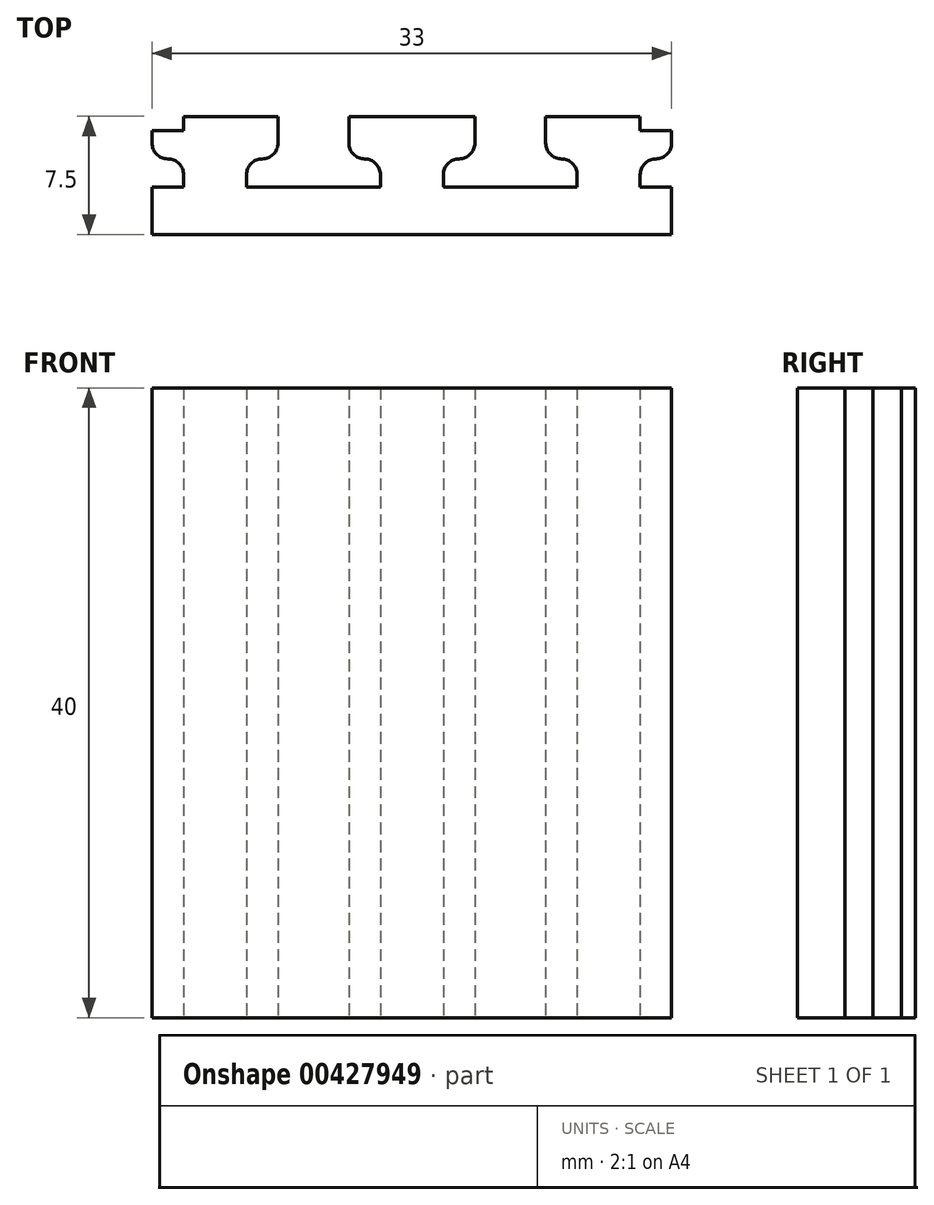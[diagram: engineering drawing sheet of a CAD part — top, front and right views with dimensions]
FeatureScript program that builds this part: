
annotation { "Feature Type Name" : "Feature", "Feature Type Description" : "" }
export const myFeature = defineFeature(function(context is Context, id is Id, definition is map)
    precondition{}
    {
        {
            var Q0;
            Q0=qCreatedBy(makeId("Top.planeOp"),FACE);
            var sketch = newSketch(context, id + "F0", { "sketchPlane" : qUnion([Q0])});
            skLineSegment(sketch, "E0.bottom", {"start": v(-2, 0.2) * mm, "end": v(2, 0.2) * mm});
            skLineSegment(sketch, "E0.top", {"start": v(-2, -3.4) * mm, "end": v(2, -3.4) * mm});
            skLineSegment(sketch, "E0.left", {"start": v(-2, 0.2) * mm, "end": v(-2, -3.4) * mm});
            skLineSegment(sketch, "E0.right", {"start": v(2, 0.2) * mm, "end": v(2, -3.4) * mm});
            skLineSegment(sketch, "E1.bottom", {"start": v(-4, 0.2) * mm, "end": v(4, 0.2) * mm});
            skLineSegment(sketch, "E1.top", {"start": v(-4, -1.6) * mm, "end": v(4, -1.6) * mm});
            skLineSegment(sketch, "E1.left", {"start": v(-4, 0.2) * mm, "end": v(-4, -1.6) * mm});
            skLineSegment(sketch, "E1.right", {"start": v(4, 0.2) * mm, "end": v(4, -1.6) * mm});
            skLineSegment(sketch, "E2.1.0.0", {"start": v(8.5, 0.2) * mm, "end": v(16.5, 0.2) * mm});
            skLineSegment(sketch, "E2.1.0.1", {"start": v(16.5, 0.2) * mm, "end": v(16.5, -1.6) * mm});
            skLineSegment(sketch, "E2.1.0.2", {"start": v(8.5, -1.6) * mm, "end": v(16.5, -1.6) * mm});
            skLineSegment(sketch, "E2.1.0.3", {"start": v(14.5, 0.2) * mm, "end": v(14.5, -3.4) * mm});
            skLineSegment(sketch, "E2.1.0.4", {"start": v(10.5, -3.4) * mm, "end": v(14.5, -3.4) * mm});
            skLineSegment(sketch, "E2.1.0.5", {"start": v(10.5, 0.2) * mm, "end": v(10.5, -3.4) * mm});
            skLineSegment(sketch, "E2.1.0.6", {"start": v(8.5, 0.2) * mm, "end": v(8.5, -1.6) * mm});
            skLineSegment(sketch, "E2.2.0.0", {"start": v(21, 0.2) * mm, "end": v(29, 0.2) * mm});
            skLineSegment(sketch, "E2.2.0.1", {"start": v(29, 0.2) * mm, "end": v(29, -1.6) * mm});
            skLineSegment(sketch, "E2.2.0.2", {"start": v(21, -1.6) * mm, "end": v(29, -1.6) * mm});
            skLineSegment(sketch, "E2.2.0.3", {"start": v(27, 0.2) * mm, "end": v(27, -3.4) * mm});
            skLineSegment(sketch, "E2.2.0.4", {"start": v(23, -3.4) * mm, "end": v(27, -3.4) * mm});
            skLineSegment(sketch, "E2.2.0.5", {"start": v(23, 0.2) * mm, "end": v(23, -3.4) * mm});
            skLineSegment(sketch, "E2.2.0.6", {"start": v(21, 0.2) * mm, "end": v(21, -1.6) * mm});
            skLineSegment(sketch, "E2.direction1", {"start": v(-4, 0.2) * mm, "end": v(8.5, 0.2) * mm, "construction": true});
            skLineSegment(sketch, "E3.bottom", {"start": v(-4, -3.4) * mm, "end": v(29, -3.4) * mm});
            skLineSegment(sketch, "E3.top", {"start": v(-4, -6.4) * mm, "end": v(29, -6.4) * mm});
            skLineSegment(sketch, "E3.left", {"start": v(-4, -3.4) * mm, "end": v(-4, -6.4) * mm});
            skLineSegment(sketch, "E3.right", {"start": v(29, -3.4) * mm, "end": v(29, -6.4) * mm});
            skLineSegment(sketch, "E4.bottom", {"start": v(16.5, 0.2) * mm, "end": v(8.5, 0.2) * mm});
            skLineSegment(sketch, "E4.top", {"start": v(16.5, 1.1) * mm, "end": v(8.5, 1.1) * mm});
            skLineSegment(sketch, "E4.left", {"start": v(16.5, 0.2) * mm, "end": v(16.5, 1.1) * mm});
            skLineSegment(sketch, "E4.right", {"start": v(8.5, 0.2) * mm, "end": v(8.5, 1.1) * mm});
            skLineSegment(sketch, "E5.bottom", {"start": v(4, 0.2) * mm, "end": v(-2, 0.2) * mm});
            skLineSegment(sketch, "E5.top", {"start": v(4, 1.1) * mm, "end": v(-2, 1.1) * mm});
            skLineSegment(sketch, "E5.left", {"start": v(4, 0.2) * mm, "end": v(4, 1.1) * mm});
            skLineSegment(sketch, "E5.right", {"start": v(-2, 0.2) * mm, "end": v(-2, 1.1) * mm});
            skPoint(sketch, "E6.oppositeSnap0", {"position": v(1, 1.1) * mm});
            skLineSegment(sketch, "E6.bottom", {"start": v(21, 0.2) * mm, "end": v(27, 0.2) * mm});
            skLineSegment(sketch, "E6.top", {"start": v(21, 1.1) * mm, "end": v(27, 1.1) * mm});
            skLineSegment(sketch, "E6.left", {"start": v(21, 0.2) * mm, "end": v(21, 1.1) * mm});
            skLineSegment(sketch, "E6.right", {"start": v(27, 0.2) * mm, "end": v(27, 1.1) * mm});
            skSolve(sketch);
        }
        {
            var Q0;
            Q0 = qSketchRegion(id + "F0", true);
            extrude(context, id + "F1", {"entities" : qUnion([Q0]), "depth" : 40 * mm, "offsetDistance" : 25 * mm, "symmetric" : true});
        }
        {
            var Q0;
            Q0=makeQuery(id+"F1.opExtrude","SWEPT_EDGE",EDGE,{"disambiguationData":[OSD([sQuery(id+"F0.wireOp",EDGE,"E0.left"),sQuery(id+"F0.wireOp",EDGE,"E1.top")])]});
            var Q1;
            Q1=makeQuery(id+"F1.opExtrude","SWEPT_EDGE",EDGE,{"disambiguationData":[OSD([sQuery(id+"F0.wireOp",EDGE,"E0.right"),sQuery(id+"F0.wireOp",EDGE,"E1.top")])]});
            var Q2;
            Q2=makeQuery(id+"F1.opExtrude","SWEPT_EDGE",EDGE,{"disambiguationData":[OSD([sQuery(id+"F0.wireOp",EDGE,"E2.1.0.2"),sQuery(id+"F0.wireOp",EDGE,"E2.1.0.5")])]});
            var Q3;
            Q3=makeQuery(id+"F1.opExtrude","SWEPT_EDGE",EDGE,{"disambiguationData":[OSD([sQuery(id+"F0.wireOp",EDGE,"E2.1.0.2"),sQuery(id+"F0.wireOp",EDGE,"E2.1.0.3")])]});
            var Q4;
            Q4=makeQuery(id+"F1.opExtrude","SWEPT_EDGE",EDGE,{"disambiguationData":[OSD([sQuery(id+"F0.wireOp",EDGE,"E2.2.0.2"),sQuery(id+"F0.wireOp",EDGE,"E2.2.0.5")])]});
            var Q5;
            Q5=makeQuery(id+"F1.opExtrude","SWEPT_EDGE",EDGE,{"disambiguationData":[OSD([sQuery(id+"F0.wireOp",EDGE,"E2.2.0.2"),sQuery(id+"F0.wireOp",EDGE,"E2.2.0.3")])]});
            var Q6;
            Q6=makeQuery(id+"F1.opExtrude","SWEPT_EDGE",EDGE,{"disambiguationData":[OSD([sQuery(id+"F0.wireOp",EDGE,"E2.1.0.2"),sQuery(id+"F0.wireOp",EDGE,"E2.1.0.6")])]});
            var Q7;
            Q7=makeQuery(id+"F1.opExtrude","SWEPT_EDGE",EDGE,{"disambiguationData":[OSD([sQuery(id+"F0.wireOp",EDGE,"E1.top"),sQuery(id+"F0.wireOp",EDGE,"E1.left")])]});
            var Q8;
            Q8=makeQuery(id+"F1.opExtrude","SWEPT_EDGE",EDGE,{"disambiguationData":[OSD([sQuery(id+"F0.wireOp",EDGE,"E2.2.0.2"),sQuery(id+"F0.wireOp",EDGE,"E2.2.0.6")])]});
            var Q9;
            Q9=makeQuery(id+"F1.opExtrude","SWEPT_EDGE",EDGE,{"disambiguationData":[OSD([sQuery(id+"F0.wireOp",EDGE,"E2.1.0.1"),sQuery(id+"F0.wireOp",EDGE,"E2.1.0.2")])]});
            var Q10;
            Q10=makeQuery(id+"F1.opExtrude","SWEPT_EDGE",EDGE,{"disambiguationData":[OSD([sQuery(id+"F0.wireOp",EDGE,"E2.2.0.1"),sQuery(id+"F0.wireOp",EDGE,"E2.2.0.2")])]});
            var Q11;
            Q11=makeQuery(id+"F1.opExtrude","SWEPT_EDGE",EDGE,{"disambiguationData":[OSD([sQuery(id+"F0.wireOp",EDGE,"E1.top"),sQuery(id+"F0.wireOp",EDGE,"E1.right")])]});
            fillet(context, id + "F2", {"entities" : qUnion([Q0, Q1, Q2, Q3, Q4, Q5, Q6, Q7, Q8, Q9, Q10, Q11]), "radius" : 1 * mm, "allowEdgeOverflow" : false});
        }
    });
